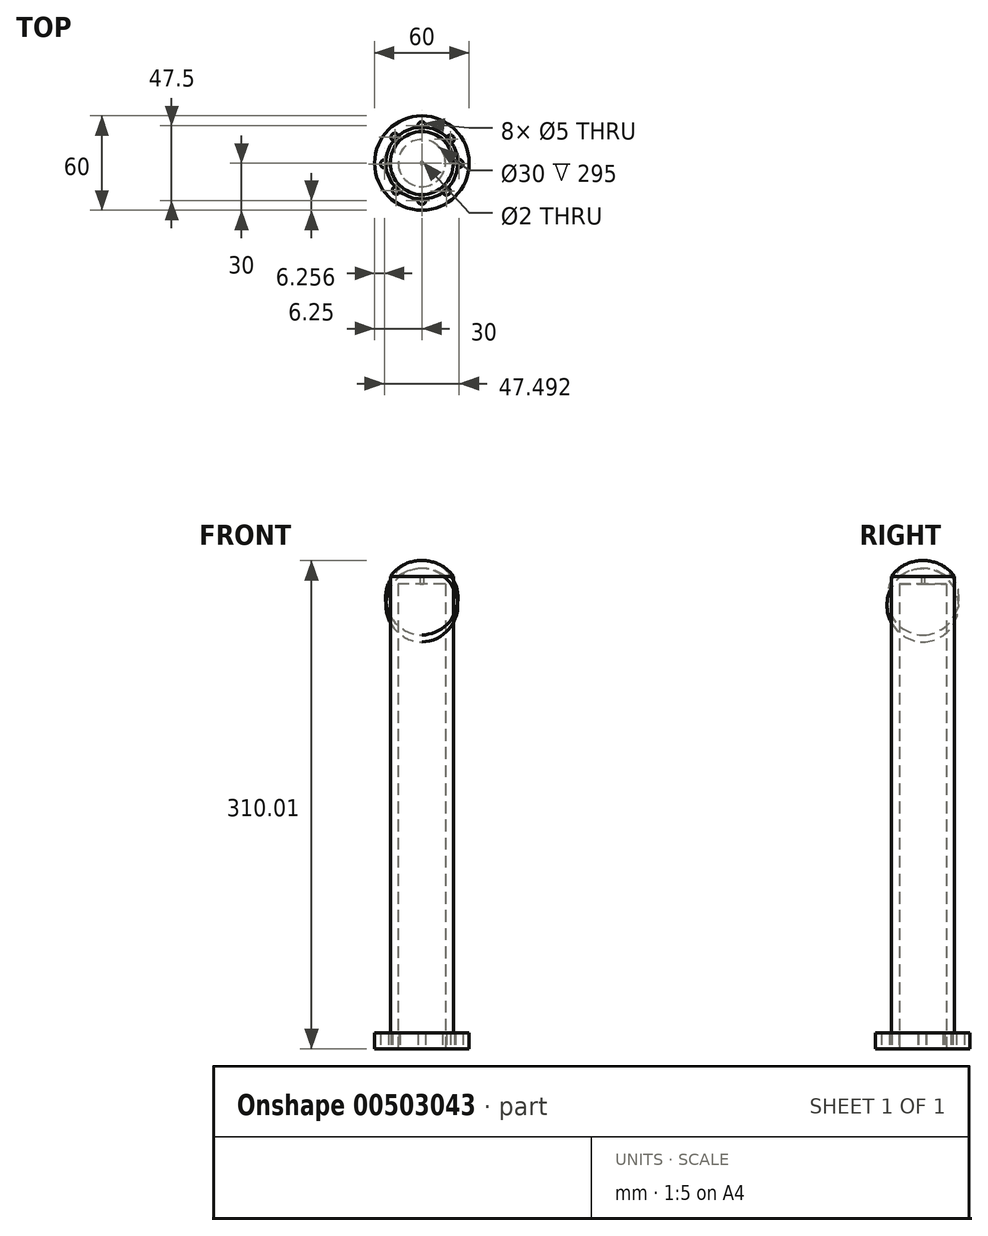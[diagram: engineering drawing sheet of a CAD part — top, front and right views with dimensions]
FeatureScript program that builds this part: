
annotation { "Feature Type Name" : "Feature", "Feature Type Description" : "" }
export const myFeature = defineFeature(function(context is Context, id is Id, definition is map)
    precondition{}
    {
        {
            var Q0;
            Q0=qCreatedBy(makeId("Top.planeOp"),FACE);
            var sketch = newSketch(context, id + "F0", { "sketchPlane" : qUnion([Q0])});
            skCircle(sketch, "E0", {"center": v(0, 0) * mm, "radius": 20 * mm});
            skSolve(sketch);
        }
        {
            var Q0;
            Q0=makeQuery(id+"F0.imprint","IMPRINT",FACE,{"disambiguationData":[TD([[makeQuery(id+"F0.imprint","IMPRINT",EDGE,{"derivedFrom":sQuery(id+"F0.wireOp",EDGE,"E0")}),1.0]])]});
            extrude(context, id + "F1", {"entities" : qUnion([Q0]), "depth" : 300 * mm});
        }
        {
            var Q0;
            Q0=qCreatedBy(makeId("Top.planeOp"),FACE);
            var sketch = newSketch(context, id + "F2", { "sketchPlane" : qUnion([Q0])});
            skCircle(sketch, "E1", {"center": v(0, 0) * mm, "radius": 15 * mm});
            skSolve(sketch);
        }
        {
            var Q0;
            Q0=makeQuery(id+"F2.imprint","IMPRINT",FACE,{"disambiguationData":[TD([[makeQuery(id+"F2.imprint","IMPRINT",EDGE,{"derivedFrom":sQuery(id+"F2.wireOp",EDGE,"E1")}),1.0]])]});
            extrude(context, id + "F3", {"entities" : qUnion([Q0]), "operationType" : NewBodyOperationType.REMOVE, "depth" : 295 * mm});
        }
        {
            var Q0;
            Q0=makeQuery(id+"F3.boolean.opBoolean","COPY",FACE,{"derivedFrom":makeQuery(id+"F3.opExtrude","CAP_FACE",FACE,{"disambiguationData":[OSD([sQuery(id+"F2.wireOp",EDGE,"E1")])],"isStart":false})});
            var sketch = newSketch(context, id + "F4", { "sketchPlane" : qUnion([Q0])});
            skCircle(sketch, "E2", {"center": v(0, 0) * mm, "radius": 1 * mm});
            skSolve(sketch);
        }
        {
            var Q0;
            Q0=makeQuery(id+"F4.imprint","IMPRINT",FACE,{"disambiguationData":[TD([[makeQuery(id+"F4.imprint","IMPRINT",EDGE,{"derivedFrom":sQuery(id+"F4.wireOp",EDGE,"E2")}),1.0]])]});
            extrude(context, id + "F5", {"entities" : qUnion([Q0]), "operationType" : NewBodyOperationType.REMOVE, "oppositeDirection" : true, "depth" : 300 * mm});
        }
        {
            var Q0;
            Q0=qCreatedBy(makeId("Front.planeOp"),FACE);
            var sketch = newSketch(context, id + "F6", { "sketchPlane" : qUnion([Q0])});
            skLineSegment(sketch, "E3", {"start": v(0, 300) * mm, "end": v(0, 310) * mm});
            skSolve(sketch);
        }
        {
            var Q0;
            Q0=qCreatedBy(makeId("Front.planeOp"),FACE);
            var sketch = newSketch(context, id + "F7", { "sketchPlane" : qUnion([Q0])});
            skArc(sketch, "E4", {"start": v(0, 310) * mm, "mid": v(-11.24, 307.5) * mm, "end": v(-19.97, 300) * mm});
            skLineSegment(sketch, "E5", {"start": v(-19.97, 300) * mm, "end": v(-14.97, 300) * mm});
            skLineSegment(sketch, "E6", {"start": v(0, 310) * mm, "end": v(0, 305) * mm});
            skArc(sketch, "E7", {"start": v(0, 305) * mm, "mid": v(-7.92, 303.8) * mm, "end": v(-14.97, 300) * mm});
            skSolve(sketch);
        }
        {
            var Q0;
            Q0 = qSketchRegion(id + "F7", true);
            var Q1;
            Q1=sQuery(id+"F6.wireOp",EDGE,"E3");
            revolve(context, id + "F8", {"operationType" : NewBodyOperationType.ADD, "entities" : qUnion([Q0]), "axis" : qUnion([Q1]), "revolveType" : RevolveType.FULL});
        }
        {
            var Q0;
            Q0=makeQuery(id+"F1.opExtrude","CAP_FACE",FACE,{"disambiguationData":[OSD([sQuery(id+"F0.wireOp",EDGE,"E0")])],"isStart":true});
            var sketch = newSketch(context, id + "F9", { "sketchPlane" : qUnion([Q0])});
            skCircle(sketch, "E8", {"center": v(0, 0) * mm, "radius": 25 * mm});
            skSolve(sketch);
        }
        {
            var Q0;
            Q0 = qSketchRegion(id + "F9", true);
            extrude(context, id + "F10", {"entities" : qUnion([Q0]), "oppositeDirection" : true, "depth" : 10 * mm});
        }
        {
            var Q0;
            Q0=makeQuery(id+"F10.opExtrude","SWEPT_BODY",BODY,{"disambiguationData":[OSD([sQuery(id+"F9.wireOp",EDGE,"E8")])]});
            deleteBodies(context, id + "F11", {"entities" : qUnion([Q0])});
        }
        {
            var Q0;
            Q0=makeQuery(id+"F1.opExtrude","CAP_FACE",FACE,{"disambiguationData":[OSD([sQuery(id+"F0.wireOp",EDGE,"E0")])],"isStart":true});
            var sketch = newSketch(context, id + "F12", { "sketchPlane" : qUnion([Q0])});
            skCircle(sketch, "E9", {"center": v(0, 0) * mm, "radius": 30 * mm});
            skCircle(sketch, "E10", {"center": v(0, 0) * mm, "radius": 15 * mm});
            skSolve(sketch);
        }
        {
            var Q0;
            Q0 = qSketchRegion(id + "F12", true);
            var Q1;
            Q1=sQuery(id+"F12.wireOp",EDGE,"E9");
            extrude(context, id + "F13", {"entities" : qUnion([Q0]), "operationType" : NewBodyOperationType.ADD, "surfaceEntities" : qUnion([Q1]), "oppositeDirection" : true, "depth" : 10 * mm});
        }
        {
            var Q0;
            Q0=makeQuery(id+"F13.boolean.opBoolean","MERGE",FACE,{"derivedFrom":[makeQuery(id+"F1.opExtrude","CAP_FACE",FACE,{"disambiguationData":[OSD([sQuery(id+"F0.wireOp",EDGE,"E0")])],"isStart":true}),makeQuery(id+"F13.opExtrude","CAP_FACE",FACE,{"disambiguationData":[OSD([sQuery(id+"F12.wireOp",EDGE,"E9"),sQuery(id+"F12.wireOp",EDGE,"E10")])],"isStart":true})]});
            var sketch = newSketch(context, id + "F14", { "sketchPlane" : qUnion([Q0])});
            skCircle(sketch, "E11", {"center": v(0, 23.75) * mm, "radius": 2.5 * mm});
            skCircle(sketch, "E12", {"center": v(0, -23.75) * mm, "radius": 2.5 * mm});
            skCircle(sketch, "E13", {"center": v(23.75, 0.32) * mm, "radius": 2.5 * mm});
            skCircle(sketch, "E14", {"center": v(-23.74, 0.53) * mm, "radius": 2.5 * mm});
            skCircle(sketch, "E15", {"center": v(-16.24, 17.33) * mm, "radius": 2.5 * mm});
            skCircle(sketch, "E16", {"center": v(18.14, -15.33) * mm, "radius": 2.5 * mm});
            skCircle(sketch, "E17", {"center": v(15.68, 17.84) * mm, "radius": 2.5 * mm});
            skCircle(sketch, "E18", {"center": v(-17.11, -16.47) * mm, "radius": 2.5 * mm});
            skSolve(sketch);
        }
        {
            var Q0;
            Q0 = qSketchRegion(id + "F14", true);
            extrude(context, id + "F15", {"entities" : qUnion([Q0]), "operationType" : NewBodyOperationType.REMOVE, "oppositeDirection" : true, "depth" : 17.9 * mm});
        }
    });
